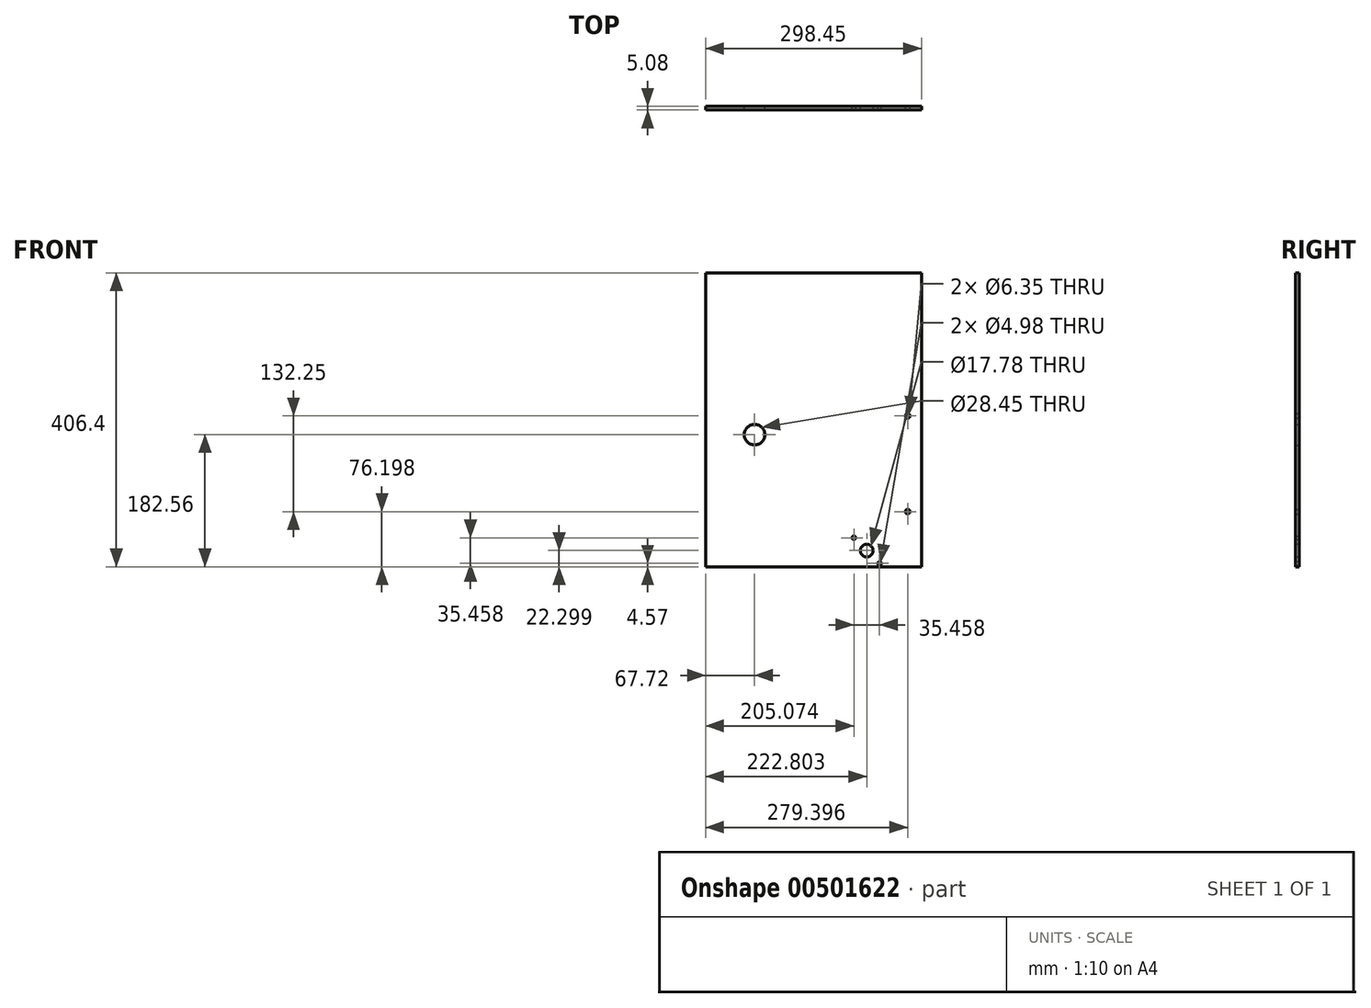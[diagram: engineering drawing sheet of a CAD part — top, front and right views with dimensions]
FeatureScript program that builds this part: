
annotation { "Feature Type Name" : "Feature", "Feature Type Description" : "" }
export const myFeature = defineFeature(function(context is Context, id is Id, definition is map)
    precondition{}
    {
        {
            var Q0;
            Q0=qCreatedBy(makeId("Front.planeOp"),FACE);
            var sketch = newSketch(context, id + "F0", { "sketchPlane" : qUnion([Q0])});
            skArc(sketch, "E0", {"start": v(0, -182.56) * mm, "mid": v(161.2, -85.7) * mm, "end": v(151.35, 102.09) * mm});
            skCircle(sketch, "E1", {"center": v(0, 0) * mm, "radius": 61.91 * mm, "construction": true});
            skLineSegment(sketch, "E2", {"start": v(0, 0) * mm, "end": v(0, -231.24) * mm, "construction": true});
            skLineSegment(sketch, "E3", {"start": v(0, -182.56) * mm, "end": v(131.59, -182.56) * mm});
            skLineSegment(sketch, "E4", {"start": v(230.73, -182.56) * mm, "end": v(230.73, 102.09) * mm});
            skLineSegment(sketch, "E5", {"start": v(230.73, 102.09) * mm, "end": v(151.35, 102.09) * mm});
            skLineSegment(sketch, "E6", {"start": v(0, 0) * mm, "end": v(230.08, 0) * mm, "construction": true});
            skLineSegment(sketch, "E7", {"start": v(182.56, 0) * mm, "end": v(151.35, 102.09) * mm, "construction": true});
            skLineSegment(sketch, "E8", {"start": v(182.56, 0) * mm, "end": v(182.56, 254) * mm, "construction": true});
            skCircle(sketch, "E9", {"center": v(173.38, 82.7) * mm, "radius": 3.18 * mm, "construction": true});
            skCircle(sketch, "E10.1.0", {"center": v(191.56, 14.24) * mm, "radius": 3.18 * mm, "construction": true});
            skCircle(sketch, "E10.2.0", {"center": v(183.7, -56.16) * mm, "radius": 3.18 * mm, "construction": true});
            skCircle(sketch, "E10.3.0", {"center": v(150.85, -118.92) * mm, "radius": 3.18 * mm, "construction": true});
            skCircle(sketch, "E10.4.0", {"center": v(97.5, -165.5) * mm, "radius": 3.18 * mm, "construction": true});
            skLineSegment(sketch, "E10.anchor1", {"start": v(0, 0) * mm, "end": v(173.38, 82.7) * mm, "construction": true});
            skLineSegment(sketch, "E10.anchor2", {"start": v(0, 0) * mm, "end": v(97.5, -165.5) * mm, "construction": true});
            skLineSegment(sketch, "E11.bottom", {"start": v(132.22, -137.96) * mm, "end": v(177.94, -137.96) * mm, "construction": true});
            skLineSegment(sketch, "E11.left", {"start": v(131.59, -138.6) * mm, "end": v(131.59, -182.56) * mm, "construction": true});
            skLineSegment(sketch, "E11.right", {"start": v(178.58, -138.6) * mm, "end": v(178.58, -182.56) * mm, "construction": true});
            skLineSegment(sketch, "E12", {"start": v(155.08, -137.96) * mm, "end": v(155.08, -182.56) * mm, "construction": true});
            skPoint(sketch, "E13", {"position": v(155.08, -160.26) * mm});
            skLineSegment(sketch, "E14.trimOffspring", {"start": v(178.58, -182.56) * mm, "end": v(230.73, -182.56) * mm});
            skPoint(sketch, "E15.visualSharp", {"position": v(131.59, -137.96) * mm});
            skArc(sketch, "E15.filletArc", {"start": v(132.22, -137.96) * mm, "mid": v(131.77, -138.15) * mm, "end": v(131.59, -138.6) * mm});
            skPoint(sketch, "E16.visualSharp", {"position": v(178.58, -137.96) * mm});
            skArc(sketch, "E16.filletArc", {"start": v(178.58, -138.6) * mm, "mid": v(178.4, -138.15) * mm, "end": v(177.94, -137.96) * mm});
            skLineSegment(sketch, "E17", {"start": v(211.68, 102.09) * mm, "end": v(211.68, -182.56) * mm, "construction": true});
            skLineSegment(sketch, "E18", {"start": v(230.73, 25.89) * mm, "end": v(180.72, 25.89) * mm, "construction": true});
            skLineSegment(sketch, "E19", {"start": v(148.38, -106.36) * mm, "end": v(230.73, -106.36) * mm, "construction": true});
            skCircle(sketch, "E20", {"center": v(211.68, -106.36) * mm, "radius": 3.18 * mm});
            skCircle(sketch, "E21", {"center": v(211.68, 25.89) * mm, "radius": 3.18 * mm});
            skLineSegment(sketch, "E22.bottom", {"start": v(230.73, -182.56) * mm, "end": v(-67.72, -182.56) * mm});
            skLineSegment(sketch, "E22.top", {"start": v(230.73, 223.84) * mm, "end": v(-67.72, 223.84) * mm});
            skLineSegment(sketch, "E22.left", {"start": v(230.73, -182.56) * mm, "end": v(230.73, 223.84) * mm});
            skLineSegment(sketch, "E22.right", {"start": v(-67.72, -182.56) * mm, "end": v(-67.72, 223.84) * mm});
            skLineSegment(sketch, "E23.bottom", {"start": v(172.81, -142.53) * mm, "end": v(137.35, -142.53) * mm, "construction": true});
            skLineSegment(sketch, "E23.top", {"start": v(172.81, -178) * mm, "end": v(137.35, -178) * mm, "construction": true});
            skLineSegment(sketch, "E23.left", {"start": v(172.81, -142.53) * mm, "end": v(172.81, -178) * mm, "construction": true});
            skLineSegment(sketch, "E23.right", {"start": v(137.35, -142.53) * mm, "end": v(137.35, -178) * mm, "construction": true});
            skCircle(sketch, "E24", {"center": v(172.81, -178) * mm, "radius": 2.49 * mm});
            skCircle(sketch, "E25", {"center": v(137.35, -142.53) * mm, "radius": 2.49 * mm});
            skCircle(sketch, "E26", {"center": v(155.08, -160.26) * mm, "radius": 8.9 * mm});
            skCircle(sketch, "E27", {"center": v(0, 0) * mm, "radius": 14.22 * mm});
            skSolve(sketch);
        }
        {
            var Q0;
            {var subQ2=sQuery(id+"F0.wireOp",EDGE,"E0");Q0=makeQuery(id+"F0.imprint","IMPRINT",FACE,{"disambiguationData":[TD([[makeQuery(id+"F0.imprint","IMPRINT",EDGE,{"derivedFrom":subQ2}),1.0]])]});}
            var Q1;
            {var subQ4=sQuery(id+"F0.wireOp",EDGE,"E0");Q1=makeQuery(id+"F0.imprint","IMPRINT",FACE,{"disambiguationData":[TD([[makeQuery(id+"F0.imprint","IMPRINT",EDGE,{"derivedFrom":subQ4}),-1.0]])]});}
            extrude(context, id + "F1", {"entities" : qUnion([Q0, Q1]), "depth" : 5.08 * mm});
        }
    });
